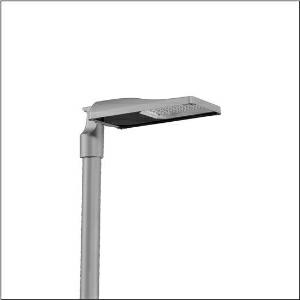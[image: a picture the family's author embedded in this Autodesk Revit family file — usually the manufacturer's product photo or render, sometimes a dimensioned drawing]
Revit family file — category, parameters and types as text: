
# Revit family: streetlight_sl_31_mini___st1_0a_5xh2d3aa08ga_e7bb
name_source: partatom
category: Lighting Fixtures
units: mm (PartAtom-declared; Revit-internal decimal feet)

## family parameters
Cut with Voids When Loaded = No
Host = Face
Light Source = No
Part Type = Normal
Room Calculation Point = No
Round Connector Dimension = Use Diameter
Shared = No

## types (1)
- --- (1 x LED, 5710 lm, 37.3 W, 3000K)
    Apparent Load = 37 VA
    CIE Flux Codes = 37 72 97 100 100
    Color Rendering = 70
    Color Temperature = 3000K
    Default Elevation = 1800 mm
    Description = Streetlight SL 31 mini Easy mast luminaire for post-top, side-entry; light control with lens of PMMA; light distribution: ST1.0a, direct asymmetric distribution, for standard-compliant lighting for roads and squares; LED: luminous flux: 5.710lm, light colour: 730, colour temperature: 3000K; luminous efficacy: 153,1lm/W; control: overheat protection, intelligent temperature release in ECG and LED module, constant luminous flux control, time-dependent luminous flux control, flexible luminous flux parameterisation, pre-setting: linear dimming characteristic; luminaire housing, of diecast aluminium, SITECO metallic grey (DB 702S), corrosivity category C5 high according to DIN EN ISO 12944; cover of toughened safety glass, transparent, mast flange of diecast aluminium, SITECO metallic grey (DB 702S), spigot size: 76/60mm, mast flange included unmounted; cable length: 6,5m, connection cable pre-assembled; mains connection: 220..240V, AC, 50/60Hz; power consumption (at start of service life): 37,3W / (at end of service life): 38,7W / (with reduced operation 50%): 17,5W; protection rating (complete): IP66; insulation class (complete): insulation class II (safety insulation); impact resistance: IK10; certification: CE, ENEC, ENEC+, VDE, UKCA; permissible operating ambient temperature for outdoor applications: -40..+50°C; packaging unit: 1 piece

Light Distribution: ST1.0a
    Height = 76 mm
    Lamp = 1 x LED
    Lamp Light Flux = 5710 lm
    Lamp Power = 37.3 W
    Lamp count = 1
    Length = 547 mm
    Luminous efficacy = 153 lm/W
    Manufacturer = Siteco
    ModVariant = No
    Model = 5XH2D3AA08GA
    Number of Poles = 1
    OnlyDefault = Yes
    Power Factor = 1
    Product Name = Streetlight SL 31 mini | ST1.0a
    Product group = mast luminaire | pylon top
    ProductGroupID = 6100
    Protection Class = Protection class II
    Protection Degree = IP 66
    RLX_Detail_Level = 1
    RLX_Emergency_Light_Flux = 0 lm
    RLX_Emergency_Type = 0
    RLX_Emergency_Type_DB = No
    RlxData = <blob elided: 39465 chars, md5=dd6d91cc>
    Socket = socket
    Standby Power = 0 W
    System Light Flux = 5710 lm
    System Power = 37 W
    Type Comments = factory setting: luminous flux: 100 % | dim-lin: 254 | 386 mA
    Type Image = l_1300326.jpg
    URL = http://relux.com
    VarID = @adj_061845
    Voltage = 0 V
    Weight = 0.00 kg
    Width = 265 mm

## geometry (parser evidence)
native form markers: Blend x4, Sweep x9
no freeform markers — native parametric forms only
